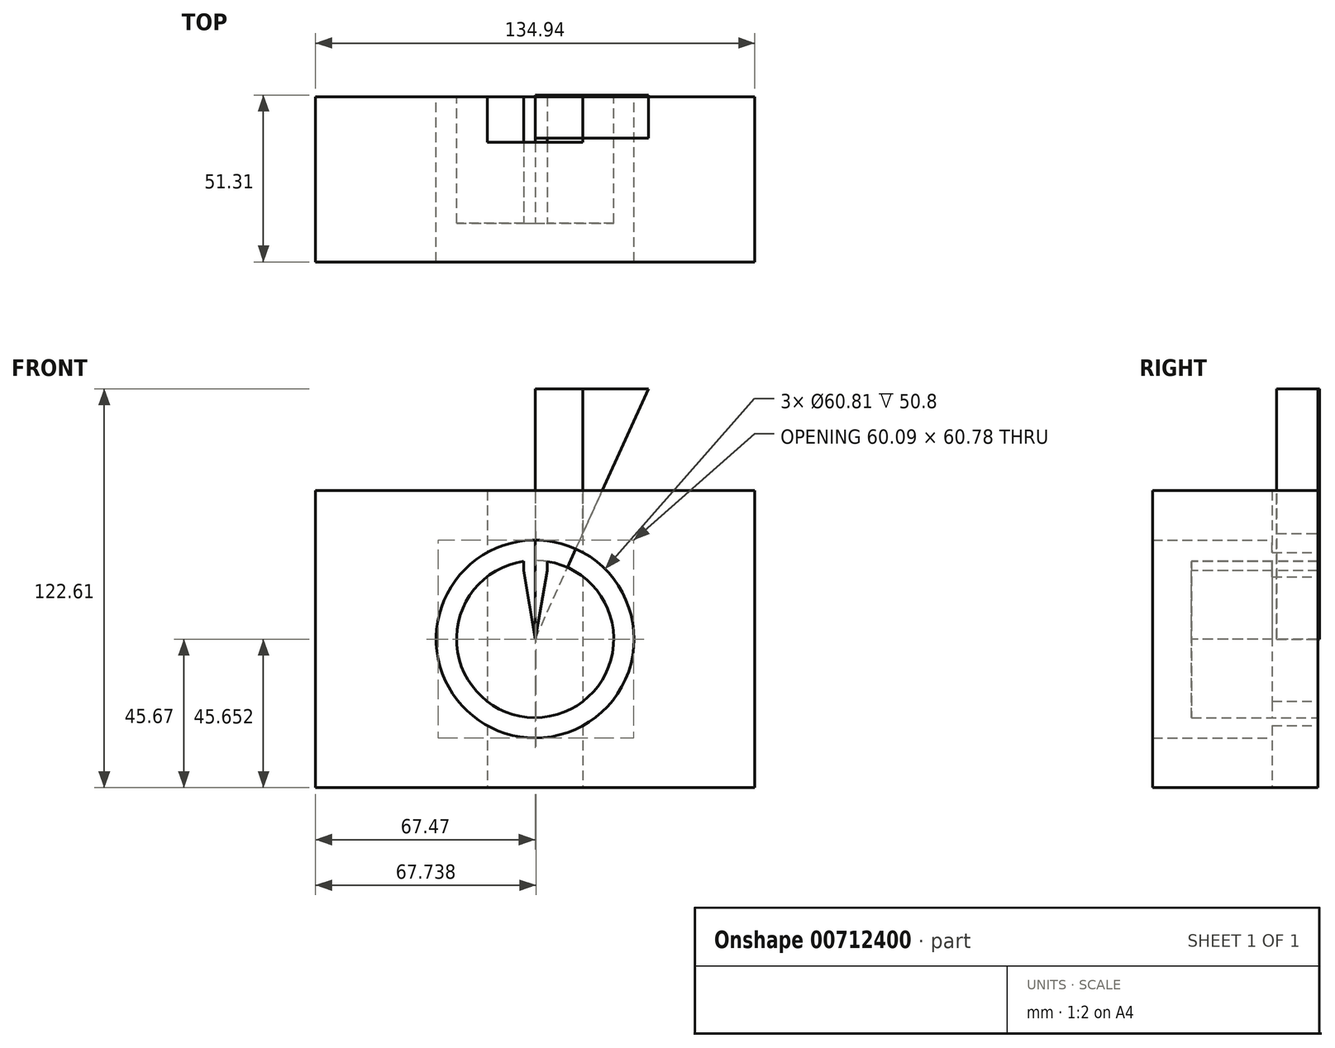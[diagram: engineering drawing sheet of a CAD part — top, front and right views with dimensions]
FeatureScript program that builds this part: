
annotation { "Feature Type Name" : "Feature", "Feature Type Description" : "" }
export const myFeature = defineFeature(function(context is Context, id is Id, definition is map)
    precondition{}
    {
        {
            var Q0;
            Q0=qCreatedBy(makeId("Front.planeOp"),FACE);
            var sketch = newSketch(context, id + "F0", { "sketchPlane" : qUnion([Q0])});
            skLineSegment(sketch, "E0.bottom", {"start": v(-67.47, 45.67) * mm, "end": v(67.47, 45.67) * mm});
            skLineSegment(sketch, "E0.top", {"start": v(-67.47, -45.67) * mm, "end": v(67.47, -45.67) * mm});
            skLineSegment(sketch, "E0.left", {"start": v(-67.47, 45.67) * mm, "end": v(-67.47, -45.67) * mm});
            skLineSegment(sketch, "E0.right", {"start": v(67.47, 45.67) * mm, "end": v(67.47, -45.67) * mm});
            skPoint(sketch, "E0.middle", {"position": v(0, 0) * mm});
            skCircle(sketch, "E1", {"center": v(0, 0) * mm, "radius": 30.4 * mm});
            skSolve(sketch);
        }
        {
            var Q0;
            Q0=makeQuery(id+"F0.imprint","IMPRINT",FACE,{"disambiguationData":[TD([[makeQuery(id+"F0.imprint","IMPRINT",EDGE,{"derivedFrom":sQuery(id+"F0.wireOp",EDGE,"E0.bottom")}),-1.0]])]});
            var Q1;
            Q1 = qSketchRegion(id + "F0", true);
            extrude(context, id + "F1", {"entities" : qUnion([Q0, Q1]), "depth" : 50.8 * mm, "offsetDistance" : 25.4 * mm});
        }
        {
            var Q0;
            Q0=qCreatedBy(makeId("Front.planeOp"),FACE);
            var sketch = newSketch(context, id + "F2", { "sketchPlane" : qUnion([Q0])});
            skLineSegment(sketch, "E2.bottom", {"start": v(-14.7, 94.92) * mm, "end": v(14.7, 94.92) * mm});
            skLineSegment(sketch, "E2.top", {"start": v(-14.7, -94.92) * mm, "end": v(14.7, -94.92) * mm});
            skLineSegment(sketch, "E2.left", {"start": v(-14.7, 94.92) * mm, "end": v(-14.7, -94.92) * mm});
            skLineSegment(sketch, "E2.right", {"start": v(14.7, 94.92) * mm, "end": v(14.7, -94.92) * mm});
            skPoint(sketch, "E2.middle", {"position": v(0, 0) * mm});
            skLineSegment(sketch, "E3.bottom", {"start": v(-14.7, 94.92) * mm, "end": v(-14.7, 94.92) * mm});
            skLineSegment(sketch, "E3.top", {"start": v(-14.7, 94.92) * mm, "end": v(-14.7, 94.92) * mm});
            skLineSegment(sketch, "E3.left", {"start": v(-14.7, 94.92) * mm, "end": v(-14.7, 94.92) * mm});
            skLineSegment(sketch, "E3.right", {"start": v(-14.7, 94.92) * mm, "end": v(-14.7, 94.92) * mm});
            skPoint(sketch, "E3.middle", {"position": v(-14.7, 94.92) * mm});
            skSolve(sketch);
        }
        {
            var Q0;
            Q0=makeQuery(id+"F2.imprint","IMPRINT",FACE,{"disambiguationData":[TD([[makeQuery(id+"F2.imprint","IMPRINT",EDGE,{"derivedFrom":sQuery(id+"F2.wireOp",EDGE,"E2.bottom")}),-1.0]])]});
            var Q1;
            Q1=sQuery(id+"F2.wireOp",EDGE,"E2.left");
            var Q2;
            Q2=sQuery(id+"F2.wireOp",EDGE,"E2.right");
            var Q3;
            Q3=sQuery(id+"F2.wireOp",EDGE,"E2.bottom");
            var Q4;
            Q4=sQuery(id+"F2.wireOp",EDGE,"E2.top");
            extrude(context, id + "F3", {"entities" : qUnion([Q0]), "operationType" : NewBodyOperationType.REMOVE, "surfaceEntities" : qUnion([Q1, Q2, Q3, Q4]), "depth" : 14.07 * mm, "offsetDistance" : 25.4 * mm});
        }
        {
            var Q0;
            Q0=qCreatedBy(makeId("Front.planeOp"),FACE);
            var sketch = newSketch(context, id + "F4", { "sketchPlane" : qUnion([Q0])});
            skCircle(sketch, "E4", {"center": v(0, 0) * mm, "radius": 24.15 * mm});
            skSolve(sketch);
        }
        {
            var Q0;
            Q0=makeQuery(id+"F4.imprint","IMPRINT",FACE,{"disambiguationData":[TD([[makeQuery(id+"F4.imprint","IMPRINT",EDGE,{"derivedFrom":sQuery(id+"F4.wireOp",EDGE,"E4")}),1.0]])]});
            extrude(context, id + "F5", {"entities" : qUnion([Q0]), "depth" : 38.86 * mm, "offsetDistance" : 25.4 * mm});
        }
        {
            var Q0;
            Q0=makeQuery(id+"F5.opExtrude","CAP_FACE",FACE,{"disambiguationData":[OSD([sQuery(id+"F4.wireOp",EDGE,"E4")])],"isStart":false});
            var sketch = newSketch(context, id + "F6", { "sketchPlane" : qUnion([Q0])});
            skLineSegment(sketch, "E5.bottom", {"start": v(0, 24.15) * mm, "end": v(0, 24.15) * mm});
            skLineSegment(sketch, "E5.top", {"start": v(0, 24.15) * mm, "end": v(0, 24.15) * mm});
            skLineSegment(sketch, "E5.left", {"start": v(0, 24.15) * mm, "end": v(0, 24.15) * mm});
            skLineSegment(sketch, "E5.right", {"start": v(0, 24.15) * mm, "end": v(0, 24.15) * mm});
            skLineSegment(sketch, "E6.bottom", {"start": v(0, 0) * mm, "end": v(0, 0) * mm});
            skLineSegment(sketch, "E6.left", {"start": v(0, 0) * mm, "end": v(0, 24.15) * mm, "construction": true});
            skLineSegment(sketch, "E6.right", {"start": v(0, 0) * mm, "end": v(0, 24.15) * mm, "construction": true});
            skLineSegment(sketch, "E7.bottom", {"start": v(0, 24.15) * mm, "end": v(-3.49, 24.15) * mm});
            skLineSegment(sketch, "E7.top", {"start": v(0, 21.06) * mm, "end": v(-3.49, 21.06) * mm});
            skLineSegment(sketch, "E7.left", {"start": v(0, 24.15) * mm, "end": v(0, 21.06) * mm});
            skLineSegment(sketch, "E7.right", {"start": v(-3.49, 24.15) * mm, "end": v(-3.49, 21.06) * mm});
            skLineSegment(sketch, "E8.bottom", {"start": v(0, 24.15) * mm, "end": v(3.67, 24.15) * mm});
            skLineSegment(sketch, "E8.top", {"start": v(0, 21.06) * mm, "end": v(3.67, 21.06) * mm});
            skLineSegment(sketch, "E8.right", {"start": v(3.67, 24.15) * mm, "end": v(3.67, 21.06) * mm});
            skLineSegment(sketch, "E9", {"start": v(0, 0) * mm, "end": v(3.67, 21.06) * mm});
            skLineSegment(sketch, "E10", {"start": v(-3.49, 21.06) * mm, "end": v(0, 0) * mm});
            skSolve(sketch);
        }
        {
            var Q0;
            Q0=makeQuery(id+"F6.imprint","IMPRINT",FACE,{"disambiguationData":[TD([[makeQuery(id+"F6.imprint","IMPRINT",EDGE,{"derivedFrom":sQuery(id+"F6.wireOp",EDGE,"E7.top")}),1.0]])]});
            var Q1;
            {var subQ0=sQuery(id+"F6.wireOp",EDGE,"E7.top");Q1=makeQuery(id+"F6.imprint","IMPRINT",FACE,{"disambiguationData":[TD([[makeQuery(id+"F6.imprint","IMPRINT",EDGE,{"derivedFrom":subQ0}),-1.0]])]});}
            var Q2;
            {var subQ0=sQuery(id+"F6.wireOp",EDGE,"E8.top");Q2=makeQuery(id+"F6.imprint","IMPRINT",FACE,{"disambiguationData":[TD([[makeQuery(id+"F6.imprint","IMPRINT",EDGE,{"derivedFrom":subQ0}),1.0]])]});}
            extrude(context, id + "F7", {"entities" : qUnion([Q0, Q1, Q2]), "operationType" : NewBodyOperationType.REMOVE, "oppositeDirection" : true, "depth" : 48 * mm, "offsetDistance" : 25.4 * mm});
        }
        {
            var Q0;
            Q0=qCreatedBy(makeId("Front.planeOp"),FACE);
            var sketch = newSketch(context, id + "F8", { "sketchPlane" : qUnion([Q0])});
            skLineSegment(sketch, "E11", {"start": v(0, 76.94) * mm, "end": v(0, 76.94) * mm});
            skLineSegment(sketch, "E12", {"start": v(0, 76.94) * mm, "end": v(0, 0) * mm});
            skLineSegment(sketch, "E13", {"start": v(0, 0) * mm, "end": v(34.84, 76.94) * mm});
            skLineSegment(sketch, "E14", {"start": v(34.84, 76.94) * mm, "end": v(0, 76.94) * mm});
            skSolve(sketch);
        }
        {
            var Q0;
            Q0=makeQuery(id+"F8.imprint","IMPRINT",FACE,{"disambiguationData":[TD([[makeQuery(id+"F8.imprint","IMPRINT",EDGE,{"derivedFrom":sQuery(id+"F8.wireOp",EDGE,"E12")}),1.0]])]});
            extrude(context, id + "F9", {"entities" : qUnion([Q0]), "depth" : 12.7 * mm, "offsetDistance" : 25.4 * mm});
        }
        {
            var Q0;
            Q0=makeQuery(id+"F9.opExtrude","CAP_FACE",FACE,{"disambiguationData":[OSD([sQuery(id+"F8.wireOp",EDGE,"E12"),sQuery(id+"F8.wireOp",EDGE,"E13"),sQuery(id+"F8.wireOp",EDGE,"E14")])],"isStart":true});
            extrude(context, id + "F10", {"entities" : qUnion([Q0]), "depth" : 0.5 * mm, "offsetDistance" : 25.4 * mm});
        }
    });
